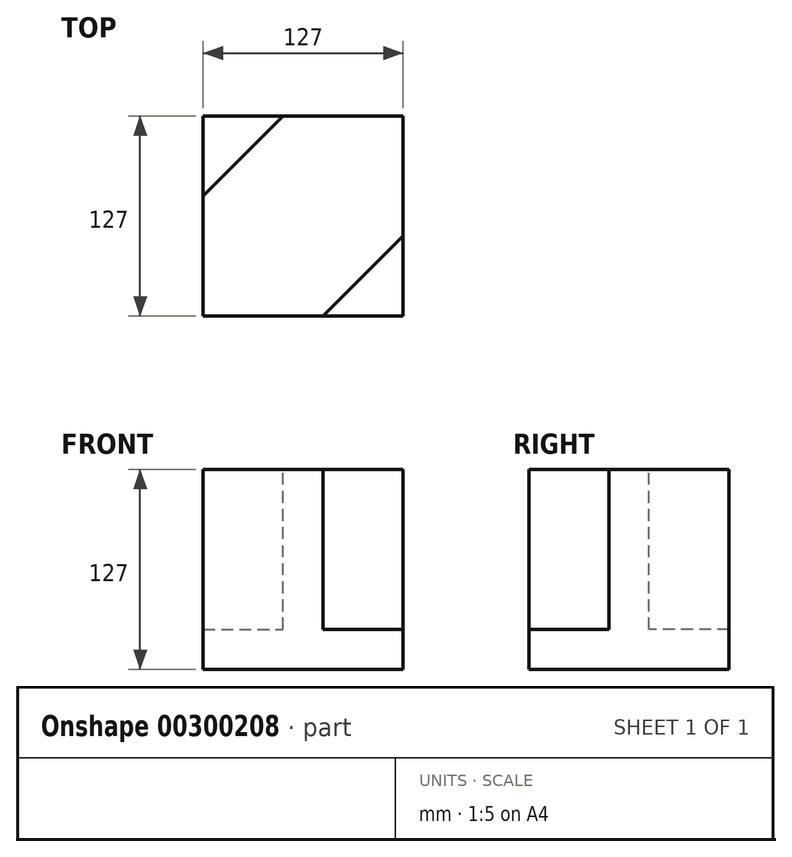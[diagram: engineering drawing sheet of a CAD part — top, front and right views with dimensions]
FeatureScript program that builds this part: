
annotation { "Feature Type Name" : "Feature", "Feature Type Description" : "" }
export const myFeature = defineFeature(function(context is Context, id is Id, definition is map)
    precondition{}
    {
        {
            var Q0;
            Q0=qCreatedBy(makeId("Top.planeOp"),FACE);
            var sketch = newSketch(context, id + "F0", { "sketchPlane" : qUnion([Q0])});
            skLineSegment(sketch, "E0.bottom", {"start": v(-63.61, 62.67) * mm, "end": v(63.39, 62.67) * mm});
            skLineSegment(sketch, "E0.top", {"start": v(-63.61, -64.33) * mm, "end": v(63.39, -64.33) * mm});
            skLineSegment(sketch, "E0.left", {"start": v(-63.61, 62.67) * mm, "end": v(-63.61, -64.33) * mm});
            skLineSegment(sketch, "E0.right", {"start": v(63.39, 62.67) * mm, "end": v(63.39, -64.33) * mm});
            skSolve(sketch);
        }
        {
            var Q0;
            Q0=makeQuery(id+"F0.imprint","IMPRINT",FACE,{"disambiguationData":[TD([[makeQuery(id+"F0.imprint","IMPRINT",EDGE,{"derivedFrom":sQuery(id+"F0.wireOp",EDGE,"E0.bottom")}),-1.0]])]});
            extrude(context, id + "F1", {"entities" : qUnion([Q0]), "endBound" : BoundingType.SYMMETRIC, "oppositeDirection" : true, "depth" : 127 * mm});
        }
        {
            var Q0;
            Q0=makeQuery(id+"F1.opExtrude","CAP_FACE",FACE,{"disambiguationData":[OSD([sQuery(id+"F0.wireOp",EDGE,"E0.bottom"),sQuery(id+"F0.wireOp",EDGE,"E0.top"),sQuery(id+"F0.wireOp",EDGE,"E0.left"),sQuery(id+"F0.wireOp",EDGE,"E0.right")])],"isStart":true});
            var sketch = newSketch(context, id + "F2", { "sketchPlane" : qUnion([Q0])});
            skLineSegment(sketch, "E1", {"start": v(-63.61, 62.67) * mm, "end": v(-12.81, 62.67) * mm});
            skLineSegment(sketch, "E2", {"start": v(-12.81, 62.67) * mm, "end": v(-63.61, 11.87) * mm});
            skLineSegment(sketch, "E3", {"start": v(-63.61, 11.87) * mm, "end": v(-63.61, 62.67) * mm});
            skLineSegment(sketch, "E4", {"start": v(63.39, 62.67) * mm, "end": v(-63.61, -64.33) * mm});
            skLineSegment(sketch, "E5.MirrorCS", {"start": v(63.39, -64.33) * mm, "end": v(63.39, -13.53) * mm});
            skLineSegment(sketch, "E6.MirrorCS", {"start": v(63.39, -13.53) * mm, "end": v(12.59, -64.33) * mm});
            skLineSegment(sketch, "E7.MirrorCS", {"start": v(12.59, -64.33) * mm, "end": v(63.39, -64.33) * mm});
            skSolve(sketch);
        }
        {
            var Q0;
            Q0=makeQuery(id+"F2.imprint","IMPRINT",FACE,{"disambiguationData":[TD([[makeQuery(id+"F2.imprint","IMPRINT",EDGE,{"derivedFrom":sQuery(id+"F2.wireOp",EDGE,"E5.MirrorCS")}),-1.0]])]});
            var Q1;
            Q1=makeQuery(id+"F2.imprint","IMPRINT",FACE,{"disambiguationData":[TD([[makeQuery(id+"F2.imprint","IMPRINT",EDGE,{"derivedFrom":sQuery(id+"F2.wireOp",EDGE,"E1")}),-1.0]])]});
            extrude(context, id + "F3", {"entities" : qUnion([Q0, Q1]), "operationType" : NewBodyOperationType.REMOVE, "oppositeDirection" : true, "depth" : 101.6 * mm});
        }
    });
